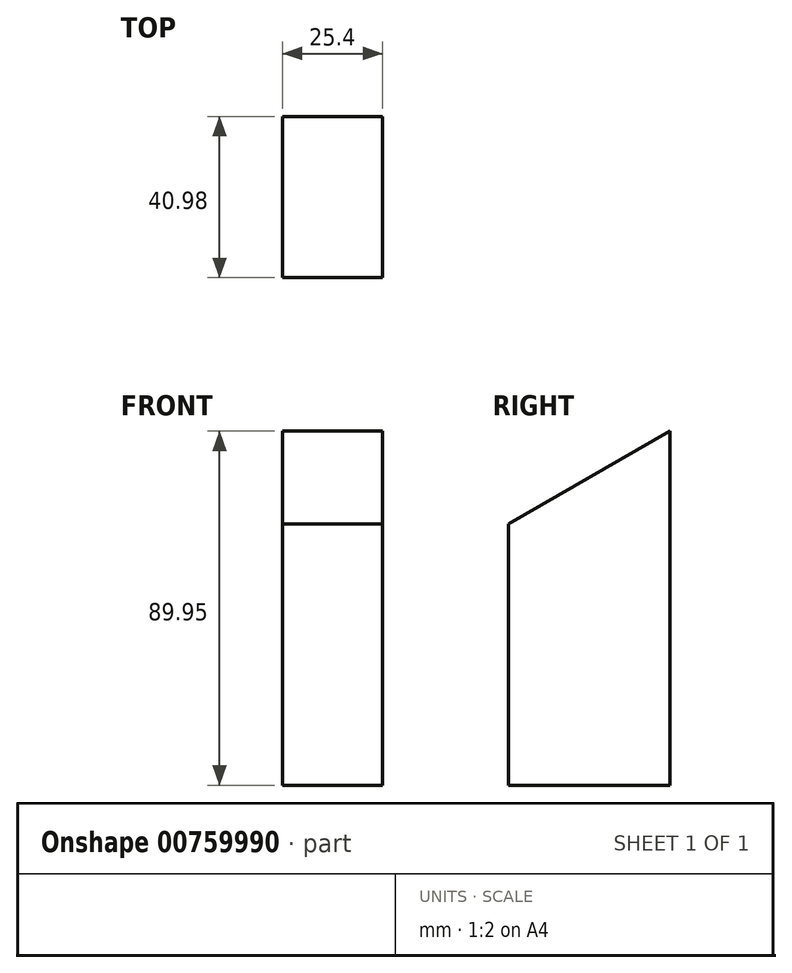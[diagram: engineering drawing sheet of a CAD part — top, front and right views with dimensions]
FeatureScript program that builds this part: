
annotation { "Feature Type Name" : "Feature", "Feature Type Description" : "" }
export const myFeature = defineFeature(function(context is Context, id is Id, definition is map)
    precondition{}
    {
        {
            var Q0;
            Q0=qCreatedBy(makeId("Right.planeOp"),FACE);
            var sketch = newSketch(context, id + "F0", { "sketchPlane" : qUnion([Q0])});
            skLineSegment(sketch, "E0", {"start": v(0, 32.98) * mm, "end": v(0, -33.38) * mm});
            skLineSegment(sketch, "E1", {"start": v(40.98, 56.57) * mm, "end": v(40.98, -33.38) * mm});
            skLineSegment(sketch, "E2", {"start": v(0, -33.38) * mm, "end": v(40.98, -33.38) * mm});
            skLineSegment(sketch, "E3", {"start": v(0, 32.98) * mm, "end": v(40.98, 56.57) * mm});
            skSolve(sketch);
        }
        {
            var Q0;
            Q0=makeQuery(id+"F0.imprint","IMPRINT",FACE,{"disambiguationData":[TD([[makeQuery(id+"F0.imprint","IMPRINT",EDGE,{"derivedFrom":sQuery(id+"F0.wireOp",EDGE,"E0")}),1.0]])]});
            extrude(context, id + "F1", {"entities" : qUnion([Q0]), "depth" : 25.4 * mm, "offsetDistance" : 25.4 * mm});
        }
    });
